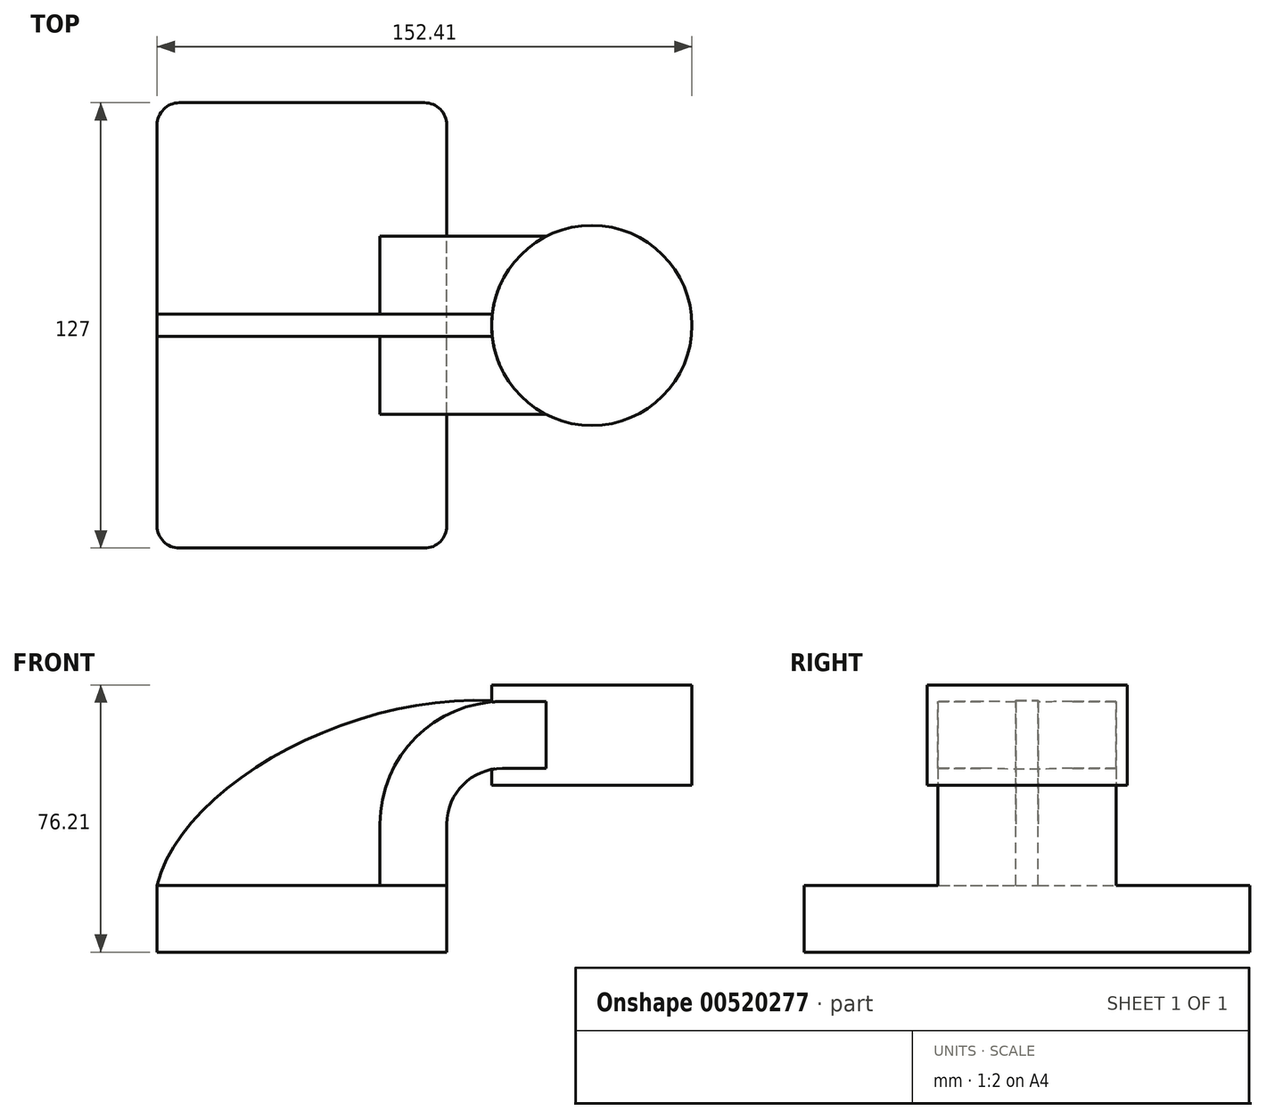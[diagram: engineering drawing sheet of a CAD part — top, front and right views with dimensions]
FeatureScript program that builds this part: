
annotation { "Feature Type Name" : "Feature", "Feature Type Description" : "" }
export const myFeature = defineFeature(function(context is Context, id is Id, definition is map)
    precondition{}
    {
        {
            var Q0;
            Q0=qCreatedBy(makeId("Front.planeOp"),FACE);
            var sketch = newSketch(context, id + "F0", { "sketchPlane" : qUnion([Q0])});
            skLineSegment(sketch, "E0.bottom", {"start": v(-41.27, -9.53) * mm, "end": v(41.28, -9.53) * mm});
            skLineSegment(sketch, "E0.top", {"start": v(-41.28, 9.53) * mm, "end": v(41.28, 9.53) * mm});
            skLineSegment(sketch, "E0.left", {"start": v(-41.28, -9.53) * mm, "end": v(-41.28, 9.53) * mm});
            skLineSegment(sketch, "E0.right", {"start": v(41.28, -9.53) * mm, "end": v(41.28, 9.53) * mm});
            skPoint(sketch, "E0.middle", {"position": v(0, 0) * mm});
            skLineSegment(sketch, "E1.bottom", {"start": v(111.13, 38.1) * mm, "end": v(60.33, 38.1) * mm});
            skLineSegment(sketch, "E1.top", {"start": v(111.13, 66.67) * mm, "end": v(60.33, 66.67) * mm});
            skLineSegment(sketch, "E1.left", {"start": v(111.13, 38.1) * mm, "end": v(111.13, 66.68) * mm});
            skLineSegment(sketch, "E1.right", {"start": v(60.33, 38.1) * mm, "end": v(60.33, 66.67) * mm});
            skPoint(sketch, "E1.middle", {"position": v(85.73, 52.39) * mm});
            skLineSegment(sketch, "E2", {"start": v(41.27, 9.53) * mm, "end": v(41.27, 27) * mm});
            skArc(sketch, "E3", {"start": v(57.15, 42.88) * mm, "mid": v(45.92, 38.23) * mm, "end": v(41.27, 27) * mm});
            skLineSegment(sketch, "E4", {"start": v(57.15, 42.88) * mm, "end": v(82.59, 42.88) * mm});
            skLineSegment(sketch, "E5.0", {"start": v(22.22, 9.53) * mm, "end": v(22.22, 27) * mm});
            skArc(sketch, "E5.1", {"start": v(57.15, 61.93) * mm, "mid": v(32.45, 51.7) * mm, "end": v(22.22, 27) * mm});
            skLineSegment(sketch, "E5.2", {"start": v(57.15, 61.93) * mm, "end": v(82.59, 61.93) * mm});
            skLineSegment(sketch, "E6", {"start": v(82.59, 61.93) * mm, "end": v(82.59, 42.88) * mm});
            skFitSpline(sketch, "E7", {"points": [v(-41.28, 9.53) * mm, v(57.15, 61.93) * mm], "startDerivative": vector(21, 86.22) * mm, "endDerivative": vector(124.8, -11.13) * mm});
            skLineSegment(sketch, "E8", {"start": v(82.59, 66.67) * mm, "end": v(82.59, 38.1) * mm});
            skSolve(sketch);
        }
        {
            var Q0;
            Q0=makeQuery(id+"F0.imprint","IMPRINT",FACE,{"disambiguationData":[TD([[makeQuery(id+"F0.imprint","IMPRINT",EDGE,{"derivedFrom":sQuery(id+"F0.wireOp",EDGE,"E0.bottom")}),1.0]])]});
            extrude(context, id + "F1", {"entities" : qUnion([Q0]), "endBound" : BoundingType.SYMMETRIC, "depth" : 127 * mm, "offsetDistance" : 25.4 * mm});
        }
        {
            var Q0;
            {var subQ2=sQuery(id+"F0.wireOp",EDGE,"E5.0");Q0=makeQuery(id+"F0.imprint","IMPRINT",FACE,{"disambiguationData":[TD([[makeQuery(id+"F0.imprint","IMPRINT",EDGE,{"derivedFrom":subQ2}),1.0]])]});}
            extrude(context, id + "F2", {"entities" : qUnion([Q0]), "operationType" : NewBodyOperationType.ADD, "endBound" : BoundingType.SYMMETRIC, "depth" : 6.35 * mm, "offsetDistance" : 25.4 * mm});
        }
        {
            var Q0;
            {var subQ0=sQuery(id+"F0.wireOp",EDGE,"E2");Q0=makeQuery(id+"F0.imprint","IMPRINT",FACE,{"disambiguationData":[TD([[makeQuery(id+"F0.imprint","IMPRINT",EDGE,{"derivedFrom":subQ0}),1.0]])]});}
            var Q1;
            {var subQ5=sQuery(id+"F0.wireOp",EDGE,"E6");Q1=makeQuery(id+"F0.imprint","IMPRINT",FACE,{"disambiguationData":[TD([[makeQuery(id+"F0.imprint","IMPRINT",EDGE,{"derivedFrom":subQ5}),-1.0]])]});}
            extrude(context, id + "F3", {"entities" : qUnion([Q0, Q1]), "operationType" : NewBodyOperationType.ADD, "endBound" : BoundingType.SYMMETRIC, "depth" : 50.8 * mm, "offsetDistance" : 25.4 * mm});
        }
        {
            var Q0;
            {var subQ0=sQuery(id+"F0.wireOp",EDGE,"E1.left");Q0=makeQuery(id+"F0.imprint","IMPRINT",FACE,{"disambiguationData":[TD([[makeQuery(id+"F0.imprint","IMPRINT",EDGE,{"derivedFrom":subQ0}),1.0]])]});}
            var Q1;
            Q1=sQuery(id+"F0.wireOp",EDGE,"E8");
            revolve(context, id + "F4", {"operationType" : NewBodyOperationType.ADD, "entities" : qUnion([Q0]), "axis" : qUnion([Q1]), "revolveType" : RevolveType.FULL});
        }
        {
            var Q0;
            {var subQ0=sQuery(id+"F0.wireOp",EDGE,"E4");var subQ1=sQuery(id+"F0.wireOp",EDGE,"E1.right");var subQ2=makeQuery(id+"F0.imprint","INTERSECT",VERTEX,{"derivedFrom":[subQ1,subQ0]});Q0=makeQuery(id+"F0.imprint","IMPRINT",FACE,{"disambiguationData":[TD([[makeQuery(id+"F0.imprint","IMPRINT",EDGE,{"disambiguationData":[TD([[subQ2,-1.0]])],"derivedFrom":subQ1}),-1.0]])]});}
            extrude(context, id + "F5", {"entities" : qUnion([Q0]), "operationType" : NewBodyOperationType.ADD, "endBound" : BoundingType.SYMMETRIC, "depth" : 50.8 * mm, "offsetDistance" : 25.4 * mm});
        }
        {
            var Q0;
            Q0=makeQuery(id+"F1.opExtrude","CAP_EDGE",EDGE,{"disambiguationData":[OSD([sQuery(id+"F0.wireOp",EDGE,"E0.right")])],"isStart":false});
            var Q1;
            Q1=makeQuery(id+"F1.opExtrude","CAP_EDGE",EDGE,{"disambiguationData":[OSD([sQuery(id+"F0.wireOp",EDGE,"E0.left")])],"isStart":false});
            var Q2;
            Q2=makeQuery(id+"F1.opExtrude","CAP_EDGE",EDGE,{"disambiguationData":[OSD([sQuery(id+"F0.wireOp",EDGE,"E0.left")])],"isStart":true});
            var Q3;
            Q3=makeQuery(id+"F1.opExtrude","CAP_EDGE",EDGE,{"disambiguationData":[OSD([sQuery(id+"F0.wireOp",EDGE,"E0.right")])],"isStart":true});
            fillet(context, id + "F6", {"entities" : qUnion([Q0, Q1, Q2, Q3]), "radius" : 6.35 * mm, "tangentPropagation" : true, "allowEdgeOverflow" : false});
        }
    });
